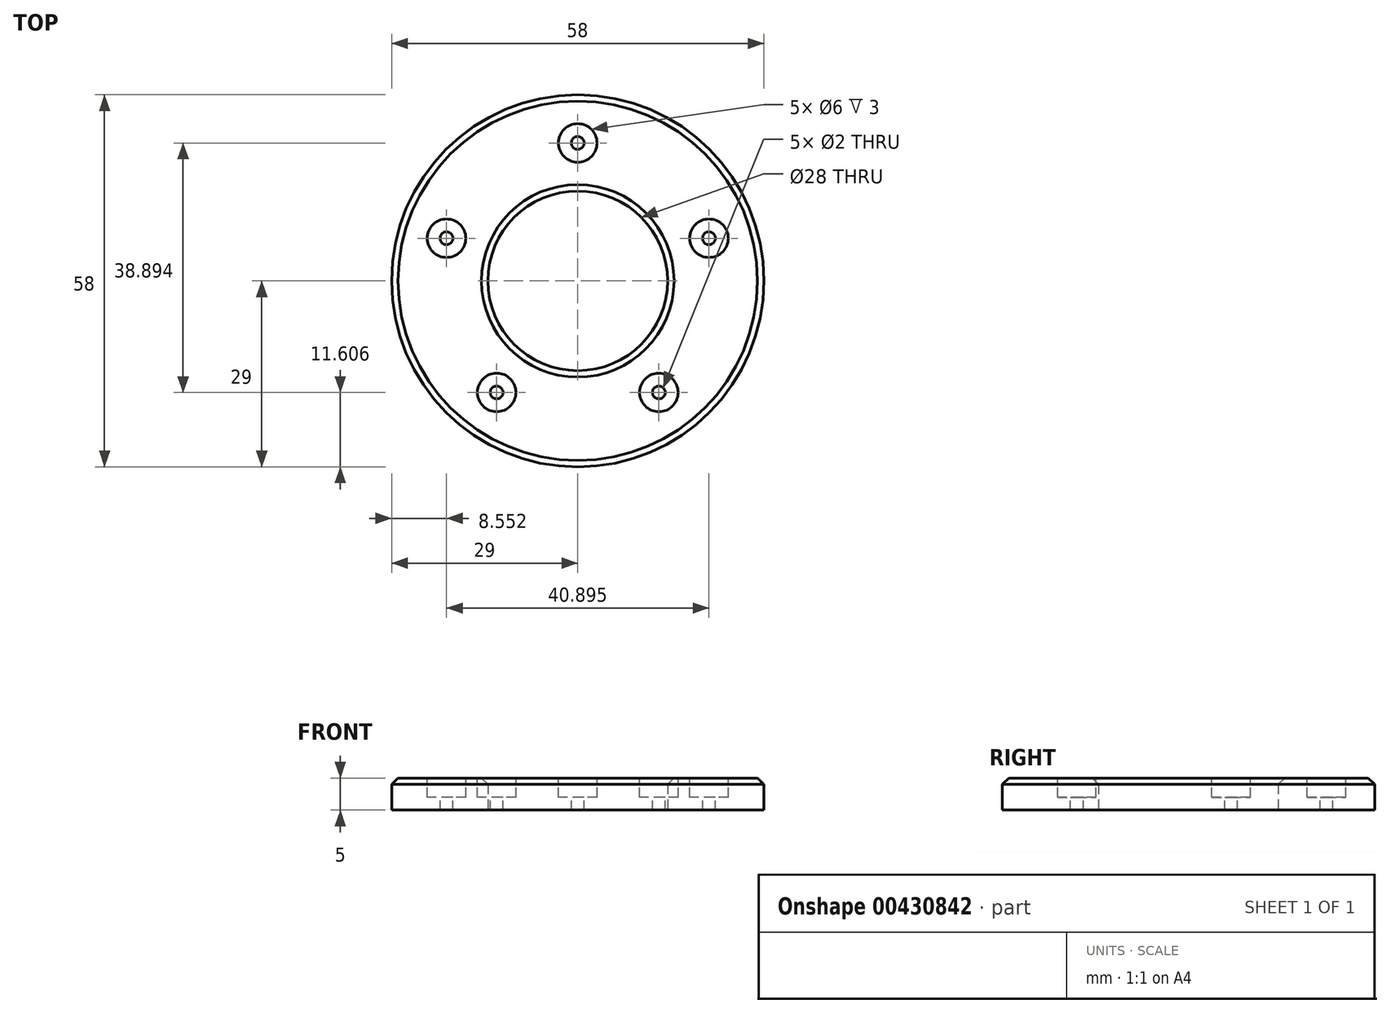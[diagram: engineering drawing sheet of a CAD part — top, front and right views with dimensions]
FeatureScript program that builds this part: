
annotation { "Feature Type Name" : "Feature", "Feature Type Description" : "" }
export const myFeature = defineFeature(function(context is Context, id is Id, definition is map)
    precondition{}
    {
        {
            var Q0;
            Q0=qCreatedBy(makeId("Top.planeOp"),FACE);
            var sketch = newSketch(context, id + "F0", { "sketchPlane" : qUnion([Q0])});
            skCircle(sketch, "E0", {"center": v(0, 0) * mm, "radius": 14 * mm});
            skCircle(sketch, "E1", {"center": v(0, 0) * mm, "radius": 29 * mm});
            skSolve(sketch);
        }
        {
            var Q0;
            Q0=makeQuery(id+"F0.imprint","IMPRINT",FACE,{"disambiguationData":[TD([[makeQuery(id+"F0.imprint","IMPRINT",EDGE,{"derivedFrom":sQuery(id+"F0.wireOp",EDGE,"E0")}),-1.0]])]});
            extrude(context, id + "F1", {"entities" : qUnion([Q0]), "depth" : 5 * mm});
        }
        {
            var Q0;
            Q0=makeQuery(id+"F1.opExtrude","CAP_FACE",FACE,{"disambiguationData":[OSD([sQuery(id+"F0.wireOp",EDGE,"E0"),sQuery(id+"F0.wireOp",EDGE,"E1")])],"isStart":false});
            var sketch = newSketch(context, id + "F2", { "sketchPlane" : qUnion([Q0])});
            skCircle(sketch, "E2", {"center": v(0, 21.5) * mm, "radius": 3 * mm});
            skCircle(sketch, "E3.1.0", {"center": v(-20.45, 6.64) * mm, "radius": 3 * mm});
            skCircle(sketch, "E3.2.0", {"center": v(-12.64, -17.4) * mm, "radius": 3 * mm});
            skCircle(sketch, "E3.3.0", {"center": v(12.64, -17.4) * mm, "radius": 3 * mm});
            skCircle(sketch, "E3.4.0", {"center": v(20.45, 6.64) * mm, "radius": 3 * mm});
            skPoint(sketch, "E3.center", {"position": v(0, 0) * mm});
            skSolve(sketch);
        }
        {
            var Q0;
            Q0 = qSketchRegion(id + "F2", true);
            extrude(context, id + "F3", {"entities" : qUnion([Q0]), "operationType" : NewBodyOperationType.REMOVE, "oppositeDirection" : true, "depth" : 3 * mm});
        }
        {
            var Q0;
            Q0=makeQuery(id+"F3.boolean.opBoolean","COPY",FACE,{"derivedFrom":makeQuery(id+"F3.opExtrude","CAP_FACE",FACE,{"disambiguationData":[OSD([sQuery(id+"F2.wireOp",EDGE,"E2")])],"isStart":false})});
            var sketch = newSketch(context, id + "F4", { "sketchPlane" : qUnion([Q0])});
            skCircle(sketch, "E4", {"center": v(0, 21.5) * mm, "radius": 1 * mm});
            skCircle(sketch, "E5.1.0", {"center": v(-20.45, 6.64) * mm, "radius": 1 * mm});
            skCircle(sketch, "E5.2.0", {"center": v(-12.64, -17.4) * mm, "radius": 1 * mm});
            skCircle(sketch, "E5.3.0", {"center": v(12.64, -17.4) * mm, "radius": 1 * mm});
            skCircle(sketch, "E5.4.0", {"center": v(20.45, 6.64) * mm, "radius": 1 * mm});
            skPoint(sketch, "E5.center", {"position": v(0, 0) * mm});
            skSolve(sketch);
        }
        {
            var Q0;
            Q0 = qSketchRegion(id + "F4", true);
            extrude(context, id + "F5", {"entities" : qUnion([Q0]), "operationType" : NewBodyOperationType.REMOVE, "oppositeDirection" : true, "depth" : 3 * mm});
        }
        {
            var Q0;
            Q0=makeQuery(id+"F1.opExtrude","CAP_EDGE",EDGE,{"disambiguationData":[OSD([sQuery(id+"F0.wireOp",EDGE,"E1")])],"isStart":false});
            var Q1;
            Q1=makeQuery(id+"F1.opExtrude","CAP_EDGE",EDGE,{"disambiguationData":[OSD([sQuery(id+"F0.wireOp",EDGE,"E0")])],"isStart":false});
            chamfer(context, id + "F6", {"entities" : qUnion([Q0, Q1]), "width" : 1 * mm, "tangentPropagation" : true});
        }
    });
